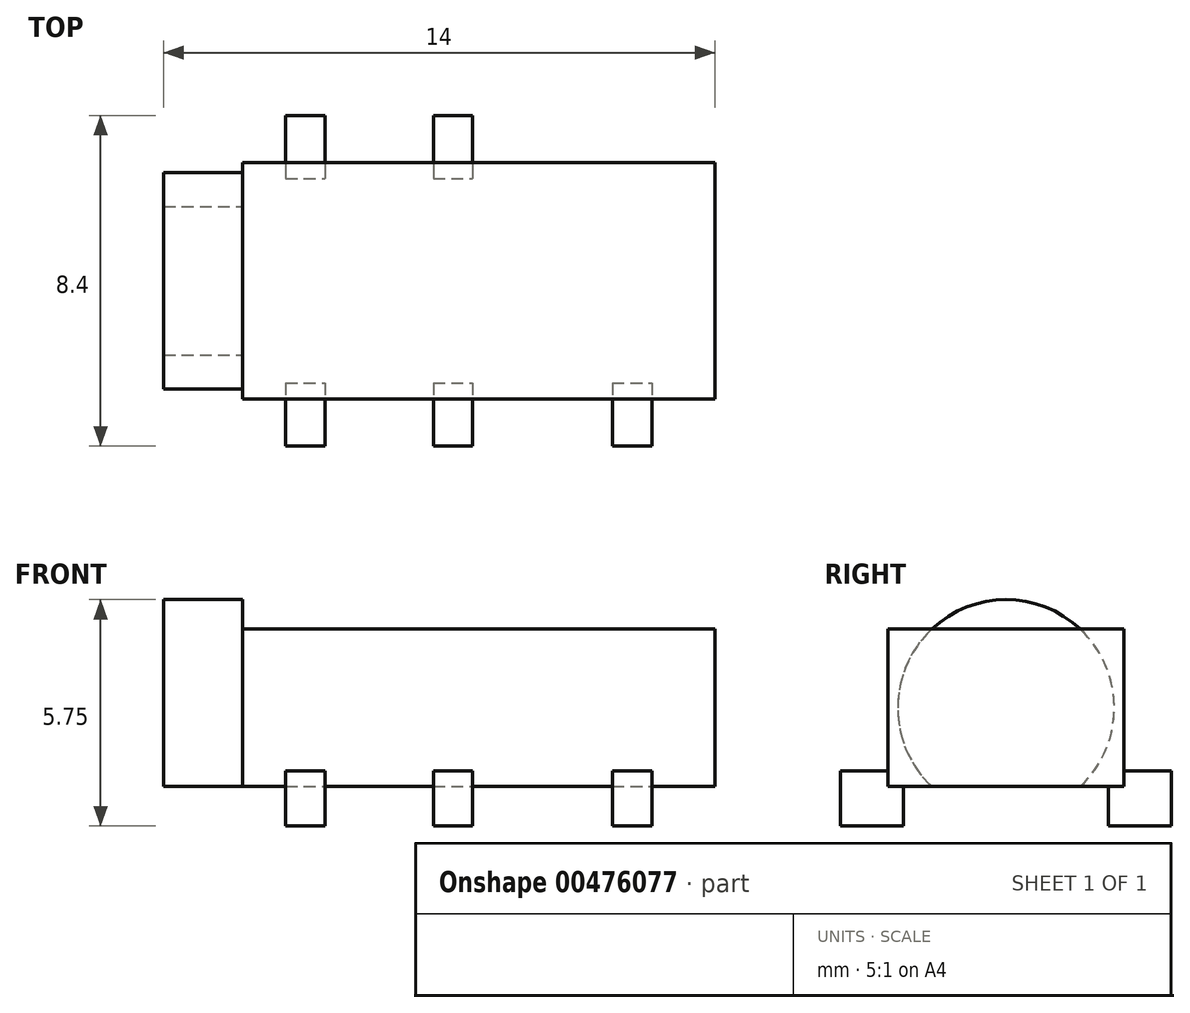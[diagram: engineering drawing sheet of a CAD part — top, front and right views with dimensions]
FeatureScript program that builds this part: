
annotation { "Feature Type Name" : "Feature", "Feature Type Description" : "" }
export const myFeature = defineFeature(function(context is Context, id is Id, definition is map)
    precondition{}
    {
        {
            var Q0;
            Q0=qCreatedBy(makeId("Top.planeOp"),FACE);
            var sketch = newSketch(context, id + "F0", { "sketchPlane" : qUnion([Q0])});
            skLineSegment(sketch, "E0", {"start": v(0, -3) * mm, "end": v(0, 3) * mm});
            skLineSegment(sketch, "E1", {"start": v(12, 3) * mm, "end": v(0, 3) * mm});
            skLineSegment(sketch, "E2", {"start": v(12, 3) * mm, "end": v(12, -3) * mm});
            skLineSegment(sketch, "E3", {"start": v(0, -3) * mm, "end": v(12, -3) * mm});
            skSolve(sketch);
        }
        {
            var Q0;
            {var subQ0=sQuery(id+"F0.wireOp",EDGE,"E2");Q0=makeQuery(id+"F0.imprint","IMPRINT",FACE,{"disambiguationData":[TD([[makeQuery(id+"F0.imprint","IMPRINT",EDGE,{"derivedFrom":subQ0}),-1.0]])]});}
            var Q1;
            {var subQ0=sQuery(id+"F0.wireOp",EDGE,"E0");Q1=makeQuery(id+"F0.imprint","IMPRINT",FACE,{"disambiguationData":[TD([[makeQuery(id+"F0.imprint","IMPRINT",EDGE,{"derivedFrom":subQ0}),-1.0]])]});}
            extrude(context, id + "F1", {"entities" : qUnion([Q0, Q1]), "depth" : 4 * mm});
        }
        {
            var Q0;
            Q0=makeQuery(id+"F1.opExtrude","SWEPT_FACE",FACE,{"disambiguationData":[OSD([sQuery(id+"F0.wireOp",EDGE,"E0")])]});
            var sketch = newSketch(context, id + "F2", { "sketchPlane" : qUnion([Q0])});
            skLineSegment(sketch, "E4", {"start": v(0, 0) * mm, "end": v(0, 4) * mm, "construction": true});
            skCircle(sketch, "E5", {"center": v(0, 2) * mm, "radius": 2.75 * mm});
            skSolve(sketch);
        }
        {
            var Q0;
            {var subQ0=sQuery(id+"F2.wireOp",EDGE,"E5");var subQ1=sQuery(id+"F0.wireOp",EDGE,"E0");var subQ2=makeQuery(id+"F1.opExtrude","CAP_EDGE",EDGE,{"disambiguationData":[OSD([subQ1])],"isStart":false});var subQ3=makeQuery(id+"F2.imprint","INTERSECT",VERTEX,{"disambiguationData":[OD(0.0)],"derivedFrom":[subQ2,subQ0]});Q0=makeQuery(id+"F2.imprint","IMPRINT",FACE,{"disambiguationData":[TD([[makeQuery(id+"F2.imprint","IMPRINT",EDGE,{"disambiguationData":[TD([[subQ3,-1.0]])],"derivedFrom":subQ0}),1.0]])]});}
            var Q1;
            {var subQ0=sQuery(id+"F2.wireOp",EDGE,"E5");var subQ1=makeQuery(id+"F1.opExtrude","CAP_EDGE",EDGE,{"disambiguationData":[OSD([sQuery(id+"F0.wireOp",EDGE,"E0")])],"isStart":false});var subQ2=makeQuery(id+"F2.imprint","INTERSECT",VERTEX,{"disambiguationData":[OD(0.0)],"derivedFrom":[subQ1,subQ0]});Q1=makeQuery(id+"F2.imprint","IMPRINT",FACE,{"disambiguationData":[TD([[makeQuery(id+"F2.imprint","IMPRINT",EDGE,{"disambiguationData":[TD([[subQ2,1.0]])],"derivedFrom":subQ0}),1.0]])]});}
            var Q2;
            {var subQ0=sQuery(id+"F2.wireOp",EDGE,"E5");var subQ1=makeQuery(id+"F1.opExtrude","CAP_EDGE",EDGE,{"disambiguationData":[OSD([sQuery(id+"F0.wireOp",EDGE,"E0")])],"isStart":true});var subQ2=makeQuery(id+"F2.imprint","INTERSECT",VERTEX,{"disambiguationData":[OD(0.0)],"derivedFrom":[subQ1,subQ0]});Q2=makeQuery(id+"F2.imprint","IMPRINT",FACE,{"disambiguationData":[TD([[makeQuery(id+"F2.imprint","IMPRINT",EDGE,{"disambiguationData":[TD([[subQ2,-1.0]])],"derivedFrom":subQ0}),1.0]])]});}
            extrude(context, id + "F3", {"entities" : qUnion([Q0, Q1, Q2]), "operationType" : NewBodyOperationType.ADD, "depth" : 2 * mm});
        }
        {
            var Q0;
            Q0=makeQuery(id+"F1.opExtrude","CAP_FACE",FACE,{"disambiguationData":[OSD([sQuery(id+"F0.wireOp",EDGE,"E0"),sQuery(id+"F0.wireOp",EDGE,"E1"),sQuery(id+"F0.wireOp",EDGE,"E2"),sQuery(id+"F0.wireOp",EDGE,"E3")])],"isStart":true});
            var sketch = newSketch(context, id + "F4", { "sketchPlane" : qUnion([Q0])});
            skLineSegment(sketch, "E6.bottom", {"start": v(1.1, -4.2) * mm, "end": v(2.1, -4.2) * mm});
            skLineSegment(sketch, "E6.top", {"start": v(1.1, -2.6) * mm, "end": v(2.1, -2.6) * mm});
            skLineSegment(sketch, "E6.left", {"start": v(1.1, -4.2) * mm, "end": v(1.1, -2.6) * mm});
            skLineSegment(sketch, "E6.right", {"start": v(2.1, -4.2) * mm, "end": v(2.1, -2.6) * mm});
            skLineSegment(sketch, "E7.bottom", {"start": v(1.1, 2.6) * mm, "end": v(2.1, 2.6) * mm});
            skLineSegment(sketch, "E7.top", {"start": v(1.1, 4.2) * mm, "end": v(2.1, 4.2) * mm});
            skLineSegment(sketch, "E7.left", {"start": v(1.1, 2.6) * mm, "end": v(1.1, 4.2) * mm});
            skLineSegment(sketch, "E7.right", {"start": v(2.1, 2.6) * mm, "end": v(2.1, 4.2) * mm});
            skLineSegment(sketch, "E8.bottom", {"start": v(4.85, 2.6) * mm, "end": v(5.85, 2.6) * mm});
            skLineSegment(sketch, "E8.top", {"start": v(4.85, 4.2) * mm, "end": v(5.85, 4.2) * mm});
            skLineSegment(sketch, "E8.left", {"start": v(4.85, 2.6) * mm, "end": v(4.85, 4.2) * mm});
            skLineSegment(sketch, "E8.right", {"start": v(5.85, 2.6) * mm, "end": v(5.85, 4.2) * mm});
            skLineSegment(sketch, "E9.bottom", {"start": v(9.4, 2.6) * mm, "end": v(10.4, 2.6) * mm});
            skLineSegment(sketch, "E9.top", {"start": v(9.4, 4.2) * mm, "end": v(10.4, 4.2) * mm});
            skLineSegment(sketch, "E9.left", {"start": v(9.4, 2.6) * mm, "end": v(9.4, 4.2) * mm});
            skLineSegment(sketch, "E9.right", {"start": v(10.4, 2.6) * mm, "end": v(10.4, 4.2) * mm});
            skLineSegment(sketch, "E10.bottom", {"start": v(4.85, -4.2) * mm, "end": v(5.85, -4.2) * mm});
            skLineSegment(sketch, "E10.top", {"start": v(4.85, -2.6) * mm, "end": v(5.85, -2.6) * mm});
            skLineSegment(sketch, "E10.left", {"start": v(4.85, -4.2) * mm, "end": v(4.85, -2.6) * mm});
            skLineSegment(sketch, "E10.right", {"start": v(5.85, -4.2) * mm, "end": v(5.85, -2.6) * mm});
            skSolve(sketch);
        }
        {
            var Q0;
            {var subQ0=sQuery(id+"F4.wireOp",EDGE,"E6.bottom");Q0=makeQuery(id+"F4.imprint","IMPRINT",FACE,{"disambiguationData":[TD([[makeQuery(id+"F4.imprint","IMPRINT",EDGE,{"derivedFrom":subQ0}),1.0]])]});}
            var Q1;
            {var subQ0=sQuery(id+"F4.wireOp",EDGE,"E7.top");Q1=makeQuery(id+"F4.imprint","IMPRINT",FACE,{"disambiguationData":[TD([[makeQuery(id+"F4.imprint","IMPRINT",EDGE,{"derivedFrom":subQ0}),-1.0]])]});}
            var Q2;
            {var subQ0=sQuery(id+"F4.wireOp",EDGE,"E7.bottom");Q2=makeQuery(id+"F4.imprint","IMPRINT",FACE,{"disambiguationData":[TD([[makeQuery(id+"F4.imprint","IMPRINT",EDGE,{"derivedFrom":subQ0}),1.0]])]});}
            var Q3;
            {var subQ0=sQuery(id+"F4.wireOp",EDGE,"E8.bottom");Q3=makeQuery(id+"F4.imprint","IMPRINT",FACE,{"disambiguationData":[TD([[makeQuery(id+"F4.imprint","IMPRINT",EDGE,{"derivedFrom":subQ0}),1.0]])]});}
            var Q4;
            {var subQ0=sQuery(id+"F4.wireOp",EDGE,"E8.top");Q4=makeQuery(id+"F4.imprint","IMPRINT",FACE,{"disambiguationData":[TD([[makeQuery(id+"F4.imprint","IMPRINT",EDGE,{"derivedFrom":subQ0}),-1.0]])]});}
            var Q5;
            {var subQ0=sQuery(id+"F4.wireOp",EDGE,"E6.top");Q5=makeQuery(id+"F4.imprint","IMPRINT",FACE,{"disambiguationData":[TD([[makeQuery(id+"F4.imprint","IMPRINT",EDGE,{"derivedFrom":subQ0}),-1.0]])]});}
            var Q6;
            {var subQ0=sQuery(id+"F4.wireOp",EDGE,"E10.bottom");Q6=makeQuery(id+"F4.imprint","IMPRINT",FACE,{"disambiguationData":[TD([[makeQuery(id+"F4.imprint","IMPRINT",EDGE,{"derivedFrom":subQ0}),1.0]])]});}
            var Q7;
            {var subQ0=sQuery(id+"F4.wireOp",EDGE,"E10.top");Q7=makeQuery(id+"F4.imprint","IMPRINT",FACE,{"disambiguationData":[TD([[makeQuery(id+"F4.imprint","IMPRINT",EDGE,{"derivedFrom":subQ0}),-1.0]])]});}
            var Q8;
            {var subQ0=sQuery(id+"F4.wireOp",EDGE,"E9.bottom");Q8=makeQuery(id+"F4.imprint","IMPRINT",FACE,{"disambiguationData":[TD([[makeQuery(id+"F4.imprint","IMPRINT",EDGE,{"derivedFrom":subQ0}),1.0]])]});}
            var Q9;
            {var subQ0=sQuery(id+"F4.wireOp",EDGE,"E9.top");Q9=makeQuery(id+"F4.imprint","IMPRINT",FACE,{"disambiguationData":[TD([[makeQuery(id+"F4.imprint","IMPRINT",EDGE,{"derivedFrom":subQ0}),-1.0]])]});}
            extrude(context, id + "F5", {"entities" : qUnion([Q0, Q1, Q2, Q3, Q4, Q5, Q6, Q7, Q8, Q9]), "operationType" : NewBodyOperationType.ADD, "depth" : 1 * mm, "hasSecondDirection" : true, "secondDirectionOppositeDirection" : true, "secondDirectionDepth" : .4 * mm});
        }
    });
